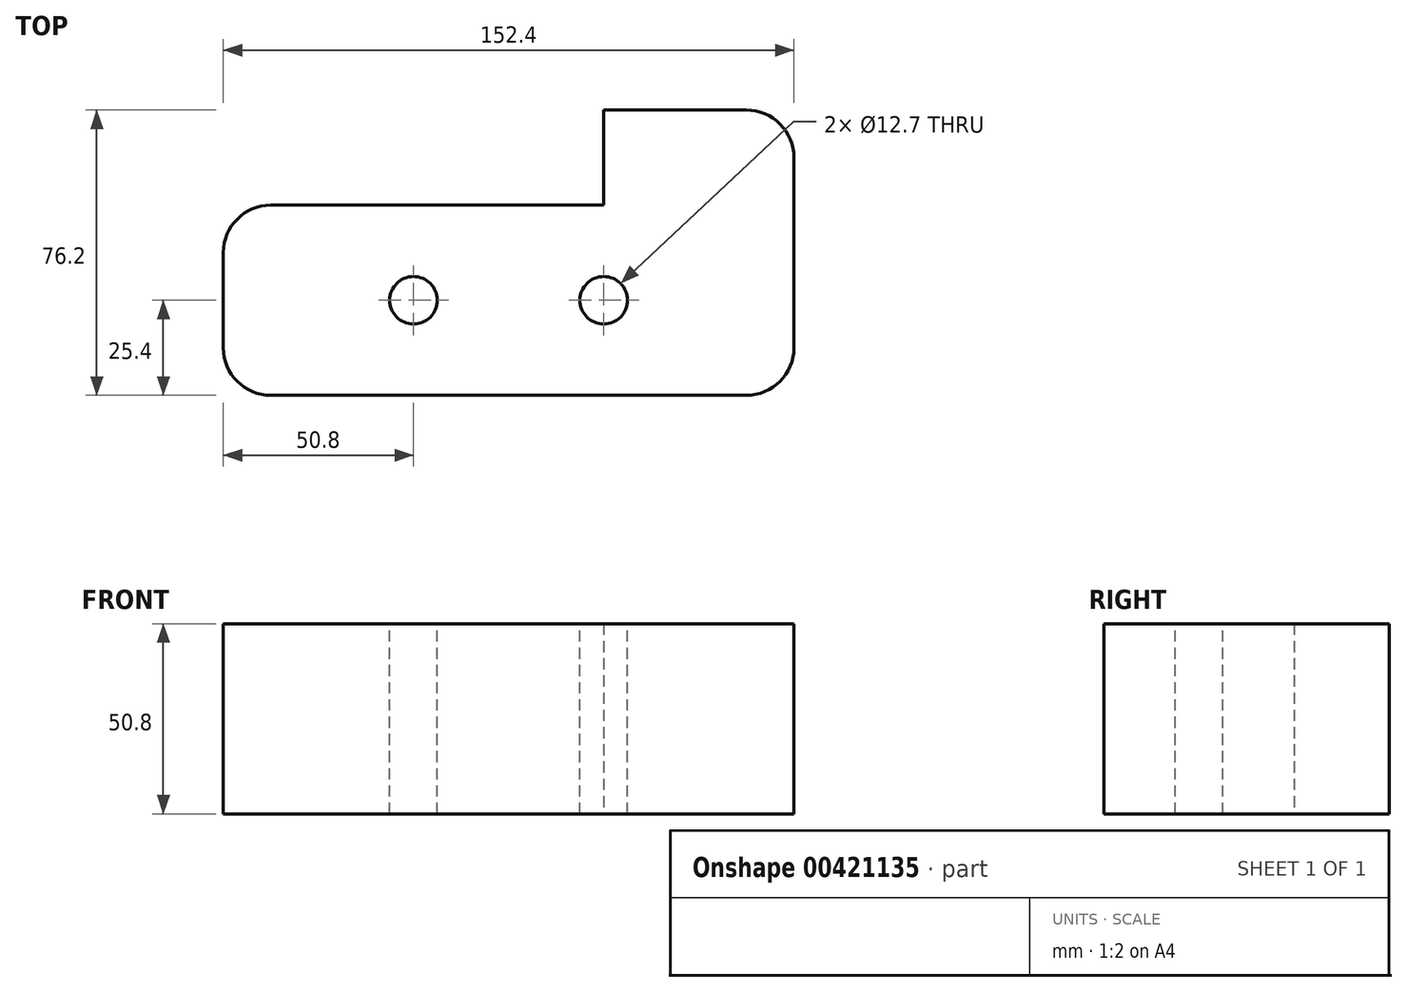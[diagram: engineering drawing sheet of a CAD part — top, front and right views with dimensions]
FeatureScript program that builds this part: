
annotation { "Feature Type Name" : "Feature", "Feature Type Description" : "" }
export const myFeature = defineFeature(function(context is Context, id is Id, definition is map)
    precondition{}
    {
        {
            var Q0;
            Q0=qCreatedBy(makeId("Top.planeOp"),FACE);
            var sketch = newSketch(context, id + "F0", { "sketchPlane" : qUnion([Q0])});
            skLineSegment(sketch, "E0", {"start": v(0, 0) * mm, "end": v(152.4, 0) * mm});
            skLineSegment(sketch, "E1", {"start": v(0, 0) * mm, "end": v(0, 50.8) * mm});
            skLineSegment(sketch, "E2", {"start": v(0, 50.8) * mm, "end": v(101.6, 50.8) * mm});
            skLineSegment(sketch, "E3", {"start": v(101.6, 50.8) * mm, "end": v(101.6, 76.2) * mm});
            skLineSegment(sketch, "E4", {"start": v(101.6, 76.2) * mm, "end": v(152.4, 76.2) * mm});
            skLineSegment(sketch, "E5", {"start": v(152.4, 76.2) * mm, "end": v(152.4, 0) * mm});
            skSolve(sketch);
        }
        {
            var Q0;
            Q0=makeQuery(id+"F0.imprint","IMPRINT",FACE,{"disambiguationData":[TD([[makeQuery(id+"F0.imprint","IMPRINT",EDGE,{"derivedFrom":sQuery(id+"F0.wireOp",EDGE,"E0")}),1.0]])]});
            extrude(context, id + "F1", {"entities" : qUnion([Q0]), "depth" : 50.8 * mm});
        }
        {
            var Q0;
            Q0=makeQuery(id+"F1.opExtrude","SWEPT_EDGE",EDGE,{"disambiguationData":[OSD([sQuery(id+"F0.wireOp",EDGE,"E0"),sQuery(id+"F0.wireOp",EDGE,"E1")])]});
            var Q1;
            Q1=makeQuery(id+"F1.opExtrude","SWEPT_EDGE",EDGE,{"disambiguationData":[OSD([sQuery(id+"F0.wireOp",EDGE,"E1"),sQuery(id+"F0.wireOp",EDGE,"E2")])]});
            var Q2;
            Q2=makeQuery(id+"F1.opExtrude","SWEPT_EDGE",EDGE,{"disambiguationData":[OSD([sQuery(id+"F0.wireOp",EDGE,"E4"),sQuery(id+"F0.wireOp",EDGE,"E5")])]});
            var Q3;
            Q3=makeQuery(id+"F1.opExtrude","SWEPT_EDGE",EDGE,{"disambiguationData":[OSD([sQuery(id+"F0.wireOp",EDGE,"E0"),sQuery(id+"F0.wireOp",EDGE,"E5")])]});
            fillet(context, id + "F2", {"entities" : qUnion([Q0, Q1, Q2, Q3]), "radius" : 12.7 * mm, "tangentPropagation" : true, "allowEdgeOverflow" : false});
        }
        {
            var Q0;
            Q0=makeQuery(id+"F1.opExtrude","CAP_FACE",FACE,{"disambiguationData":[OSD([sQuery(id+"F0.wireOp",EDGE,"E0"),sQuery(id+"F0.wireOp",EDGE,"E1"),sQuery(id+"F0.wireOp",EDGE,"E2"),sQuery(id+"F0.wireOp",EDGE,"E3"),sQuery(id+"F0.wireOp",EDGE,"E4"),sQuery(id+"F0.wireOp",EDGE,"E5")])],"isStart":false});
            var sketch = newSketch(context, id + "F3", { "sketchPlane" : qUnion([Q0])});
            skLineSegment(sketch, "E6", {"start": v(0, 25.4) * mm, "end": v(50.8, 25.4) * mm});
            skLineSegment(sketch, "E7", {"start": v(50.8, 25.4) * mm, "end": v(101.6, 25.4) * mm});
            skSolve(sketch);
        }
        {
            var Q0;
            Q0=sQuery(id+"F3.wireOp",VERTEX,"E7.start");
            var Q1;
            Q1=sQuery(id+"F3.wireOp",VERTEX,"E7.end");
            var Q2;
            Q2=makeQuery(id+"F1.opExtrude","SWEPT_BODY",BODY,{"disambiguationData":[OSD([sQuery(id+"F0.wireOp",EDGE,"E0"),sQuery(id+"F0.wireOp",EDGE,"E1"),sQuery(id+"F0.wireOp",EDGE,"E2"),sQuery(id+"F0.wireOp",EDGE,"E3"),sQuery(id+"F0.wireOp",EDGE,"E4"),sQuery(id+"F0.wireOp",EDGE,"E5")])]});
            hole(context, id + "F4", {"style" : HoleStyle.SIMPLE, "endStyle" : HoleEndStyle.THROUGH, "holeDiameter" : 12.7 * mm, "isTappedThrough" : true, "tappedDepth" : 12.7 * mm, "tapClearance" : 3, "locations" : qUnion([Q0, Q1]), "scope" : qUnion([Q2])});
        }
    });
